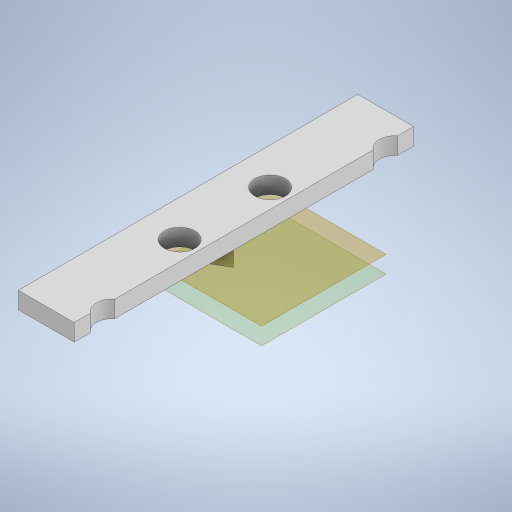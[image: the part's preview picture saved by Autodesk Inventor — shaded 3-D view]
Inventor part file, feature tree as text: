
AUTODESK INVENTOR PART (.ipt)
format: ipt  version: 2024 (Build 280153000, 153)  size: 323,072 bytes
history: native  units: mm
features: extrude x8, sketch x8, plane x3
ambient origin geometry x8: Origin, YZ Plane, XZ Plane, XY Plane, X Axis, Y Axis, Z Axis, Center Point
bodies: Body1 (feature_tree)
feature tree (19):
  plane  "Work Plane5"
  extrude  "Extrusion34"  Depth=40.0mm
  plane  "Work Plane2"
  extrude  "Extrusion35"  Depth=36.0mm
  plane  "Work Plane1"
  extrude  "Extrusion51"  Depth=2.3mm
  sketch  "Sketch77"  dims[d211=10.0mm d212=0.0mm d219=35.0mm]
  extrude  "Extrusion53"  Depth=10.0mm
  extrude  "Extrusion54"  Depth=60.0mm
  extrude  "Extrusion56"  Depth=3.0mm TaperAngle=0.0deg
  extrude  "Extrusion57"  Depth=11.5mm
  extrude  "Extrusion58"  Depth=4.5mm
  sketch  "Sketch45"  dims[d142=38.0mm d143=40.0mm]
  sketch  "Sketch47"  dims[d144=30.0mm d145=0.0mm d146=36.0mm]
  sketch  "Sketch74"  dims[d147=30.0mm d148=-2.617994mm d210=2.3mm]
  sketch  "Sketch78"  dims[d220=58.0mm d221=60.0mm]
  sketch  "Sketch81"  dims[d222=3.0mm d223=0.0mm d224=3.0mm d225=0.0mm]
  sketch  "Sketch83"  dims[d232=5.0mm d233=11.5mm]
  sketch  "Sketch84"  dims[d234=5.4mm d235=17.5mm d236=5.4mm d237=17.5mm d238=5.4mm d239=5.0mm d240=17.0mm d241=5.4mm d242=16.0mm d243=5.4mm d244=17.0mm d245=5.4mm d246=17.5mm d247=5.4mm d248=17.5mm d249=5.0mm d250=30.0mm d251=0.0mm d253=4.8mm d254=4.5mm d255=0.0mm d256=0.0mm d257=0.0mm d49=0.5mm d50=0.872665mm d51=0.5mm d52=0.872665mm d130=0.5mm d131=0.872665mm d132=0.5mm d133=0.872665mm d156=0.5mm d157=0.872665mm d158=0.5mm d159=0.872665mm d173=0.5mm d174=0.872665mm d175=0.5mm d176=0.872665mm d226=0.5mm d227=0.872665mm]
